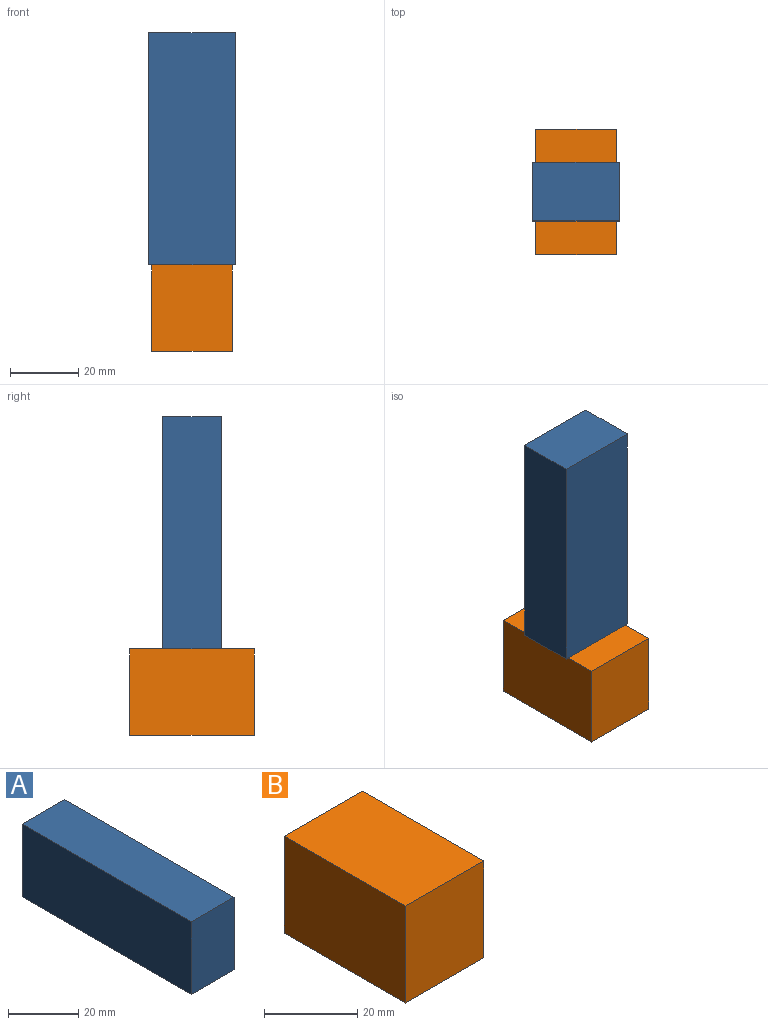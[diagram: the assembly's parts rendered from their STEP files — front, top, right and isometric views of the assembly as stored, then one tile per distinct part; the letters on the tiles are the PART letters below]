
ASSEMBLY  parts=2 mates=1
PART A: 6 faces, bbox 17.2x68.3x25.4 mm
  f0: plane 68.25x25.4mm, normal (-1,0,0), area 1733.6mm2, adj f1,f3,f4,f5
  f1: plane 25.4x17.22mm, normal (0,-1,0), area 437.4mm2, adj f0,f2,f4,f5
  f2: plane 68.25x25.4mm, normal (1,0,0), area 1733.6mm2, adj f1,f3,f4,f5
  f3: plane 25.4x17.22mm, normal (0,1,0), area 437.4mm2, adj f0,f2,f4,f5
  f4: plane 68.25x17.22mm, normal (0,0,1), area 1175.5mm2, adj f0,f1,f2,f3
  f5: plane 68.25x17.22mm, normal (0,0,-1), area 1175.5mm2, adj f0,f1,f2,f3
PART B: 6 faces, bbox 23.7x36.7x25.4 mm
  f0: plane 36.66x25.4mm, normal (-1,0,0), area 931.2mm2, adj f1,f3,f4,f5
  f1: plane 25.4x23.69mm, normal (0,-1,0), area 601.6mm2, adj f0,f2,f4,f5
  f2: plane 36.66x25.4mm, normal (1,0,0), area 931.2mm2, adj f1,f3,f4,f5
  f3: plane 25.4x23.69mm, normal (0,1,0), area 601.6mm2, adj f0,f2,f4,f5
  f4: plane 36.66x23.69mm, normal (0,0,1), area 868.4mm2, adj f0,f1,f2,f3
  f5: plane 36.66x23.69mm, normal (0,0,-1), area 868.4mm2, adj f0,f1,f2,f3
PLACE A rot(axis=(0.58,0.58,0.58),120deg) t=(-12.7,-25.91,39.91)mm
PLACE B rot(axis=(0,0,1),180deg) t=(-53.53,-46.88,-25.4)mm
MATE revolute B.f4 <-> A.f1  axis (0,0,1) through (0,0,0)mm
